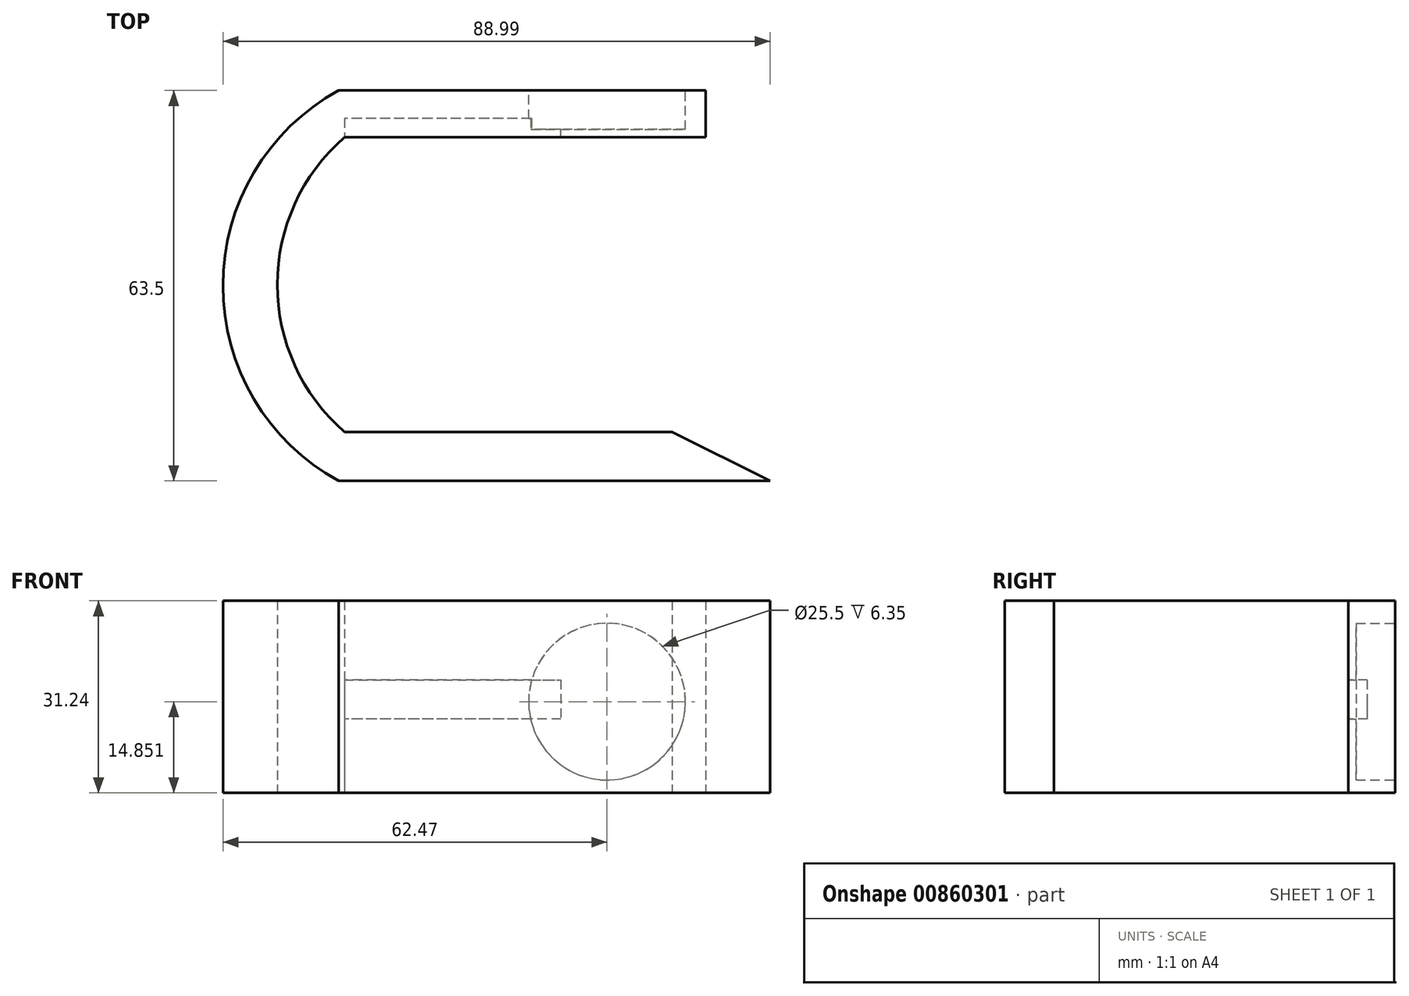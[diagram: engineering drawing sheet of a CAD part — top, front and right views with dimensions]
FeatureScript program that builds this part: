
annotation { "Feature Type Name" : "Feature", "Feature Type Description" : "" }
export const myFeature = defineFeature(function(context is Context, id is Id, definition is map)
    precondition{}
    {
        {
            var Q0;
            Q0=qCreatedBy(makeId("Top.planeOp"),FACE);
            var sketch = newSketch(context, id + "F0", { "sketchPlane" : qUnion([Q0])});
            skLineSegment(sketch, "E0", {"start": v(16.06, -7.97) * mm, "end": v(-43.66, -7.97) * mm});
            skArc(sketch, "E1", {"start": v(-43.66, 55.53) * mm, "mid": v(-62.47, 23.78) * mm, "end": v(-43.66, -7.97) * mm});
            skLineSegment(sketch, "E2", {"start": v(-43.66, 55.53) * mm, "end": v(16.06, 55.53) * mm});
            skLineSegment(sketch, "E3", {"start": v(-42.7, 47.91) * mm, "end": v(16.06, 47.91) * mm});
            skLineSegment(sketch, "E4", {"start": v(16.06, 47.91) * mm, "end": v(16.06, 55.53) * mm});
            skArc(sketch, "E5", {"start": v(-42.7, 47.91) * mm, "mid": v(-53.62, 23.96) * mm, "end": v(-42.7, 0) * mm});
            skLineSegment(sketch, "E6", {"start": v(-42.7, 0) * mm, "end": v(10.55, 0) * mm});
            skLineSegment(sketch, "E7", {"start": v(16.06, -7.97) * mm, "end": v(26.52, -7.97) * mm});
            skLineSegment(sketch, "E8", {"start": v(10.55, 0) * mm, "end": v(26.52, -7.97) * mm});
            skSolve(sketch);
        }
        {
            var Q0;
            Q0 = qSketchRegion(id + "F0", true);
            extrude(context, id + "F1", {"entities" : qUnion([Q0]), "depth" : 31.24 * mm, "offsetDistance" : 25.4 * mm});
        }
        {
            var Q0;
            Q0=makeQuery(id+"F1.opExtrude","SWEPT_FACE",FACE,{"disambiguationData":[OSD([sQuery(id+"F0.wireOp",EDGE,"E2")])]});
            var sketch = newSketch(context, id + "F2", { "sketchPlane" : qUnion([Q0])});
            skCircle(sketch, "E9", {"center": v(0, 14.85) * mm, "radius": 12.75 * mm});
            skSolve(sketch);
        }
        {
            var Q0;
            Q0 = qSketchRegion(id + "F2", true);
            extrude(context, id + "F3", {"entities" : qUnion([Q0]), "operationType" : NewBodyOperationType.REMOVE, "oppositeDirection" : true, "depth" : 6.35 * mm, "offsetDistance" : 25.4 * mm});
        }
        {
            var Q0;
            Q0=makeQuery(id+"F3.boolean.opBoolean","COPY",FACE,{"derivedFrom":makeQuery(id+"F3.opExtrude","CAP_FACE",FACE,{"disambiguationData":[OSD([sQuery(id+"F2.wireOp",EDGE,"E9")])],"isStart":false})});
            var sketch = newSketch(context, id + "F4", { "sketchPlane" : qUnion([Q0])});
            skLineSegment(sketch, "E10", {"start": v(12.26, 18.36) * mm, "end": v(7.5, 18.36) * mm});
            skLineSegment(sketch, "E11", {"start": v(7.5, 18.36) * mm, "end": v(7.5, 12.01) * mm});
            skLineSegment(sketch, "E12", {"start": v(7.5, 12.01) * mm, "end": v(12.43, 12.01) * mm});
            skSolve(sketch);
        }
        {
            var Q0;
            Q0 = qSketchRegion(id + "F4", true);
            var Q1;
            {var subQ0=sQuery(id+"F4.wireOp",EDGE,"E10");Q1=makeQuery(id+"F4.imprint","IMPRINT",FACE,{"disambiguationData":[TD([[makeQuery(id+"F4.imprint","IMPRINT",EDGE,{"derivedFrom":subQ0}),1.0]])]});}
            extrude(context, id + "F5", {"entities" : qUnion([Q0, Q1]), "operationType" : NewBodyOperationType.REMOVE, "oppositeDirection" : true, "depth" : 25.4 * mm, "offsetDistance" : 25.4 * mm});
        }
        {
            var Q0;
            Q0=makeQuery(id+"F1.opExtrude","SWEPT_FACE",FACE,{"disambiguationData":[OSD([sQuery(id+"F0.wireOp",EDGE,"E3")])]});
            var sketch = newSketch(context, id + "F6", { "sketchPlane" : qUnion([Q0])});
            skPoint(sketch, "E13.endSnap0", {"position": v(-42.7, 15.62) * mm});
            skLineSegment(sketch, "E14", {"start": v(-12.26, 18.36) * mm, "end": v(-42.7, 18.36) * mm});
            skLineSegment(sketch, "E15", {"start": v(-12.43, 12.01) * mm, "end": v(-42.7, 12.01) * mm});
            skLineSegment(sketch, "E16", {"start": v(-12.26, 18.36) * mm, "end": v(-12.43, 12.01) * mm});
            skLineSegment(sketch, "E17", {"start": v(-42.7, 12.01) * mm, "end": v(-42.7, 18.36) * mm});
            skSolve(sketch);
        }
        {
            var Q0;
            Q0 = qSketchRegion(id + "F6", true);
            extrude(context, id + "F7", {"entities" : qUnion([Q0]), "operationType" : NewBodyOperationType.REMOVE, "oppositeDirection" : true, "depth" : 3.05 * mm, "offsetDistance" : 25.4 * mm});
        }
    });
